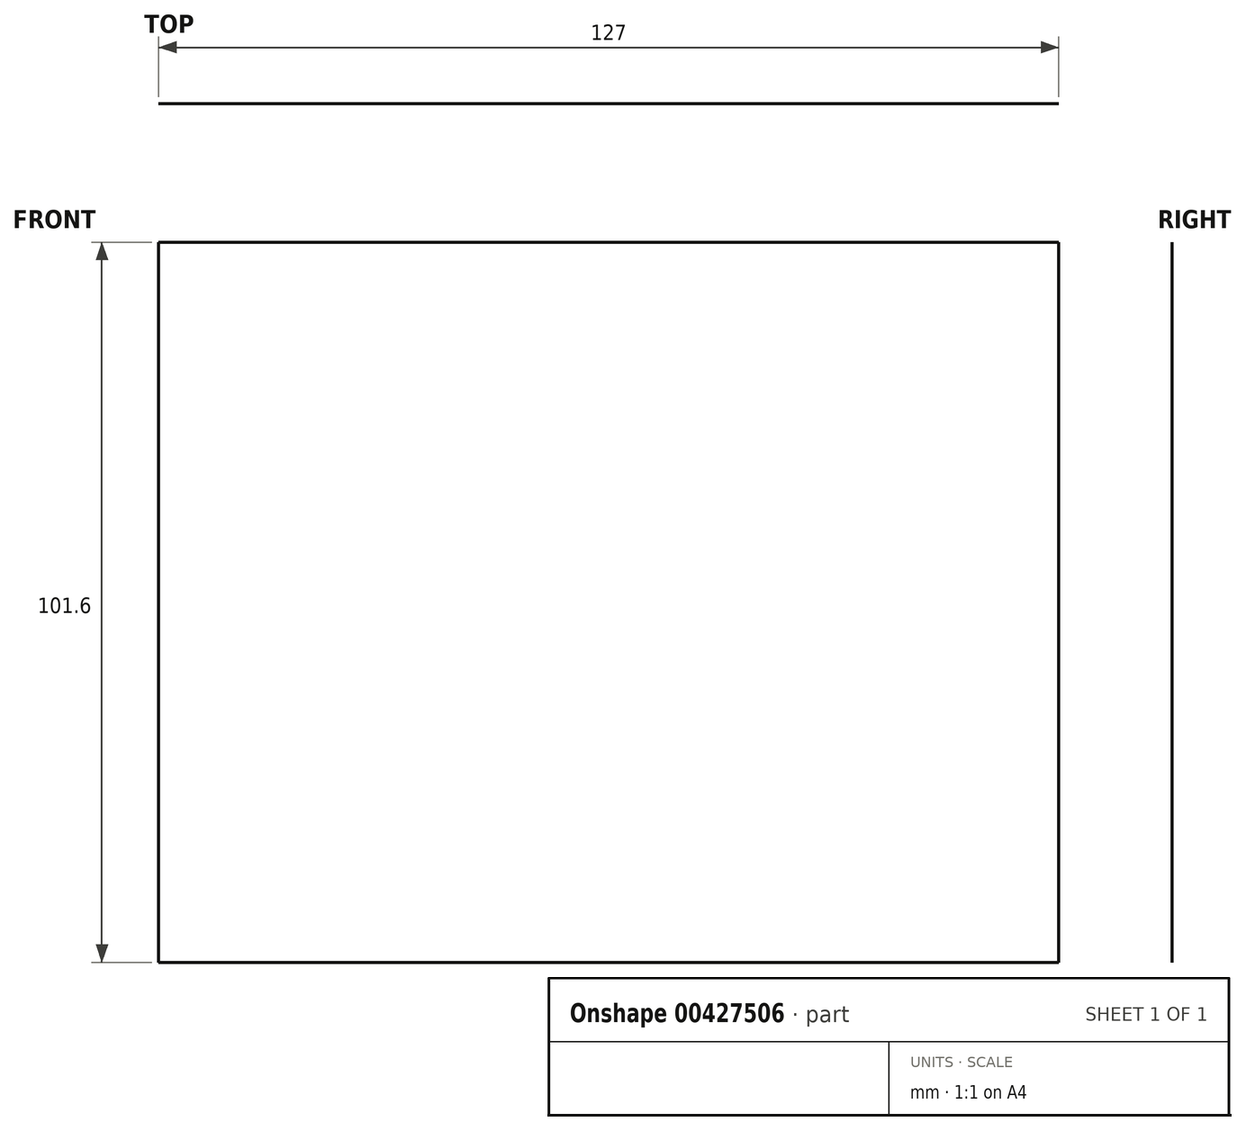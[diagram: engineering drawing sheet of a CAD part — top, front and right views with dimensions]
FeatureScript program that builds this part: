
annotation { "Feature Type Name" : "Feature", "Feature Type Description" : "" }
export const myFeature = defineFeature(function(context is Context, id is Id, definition is map)
    precondition{}
    {
        {
            var Q0;
            Q0=qCreatedBy(makeId("Top.planeOp"),FACE);
            var sketch = newSketch(context, id + "F0", { "sketchPlane" : qUnion([Q0])});
            skLineSegment(sketch, "E0.bottom", {"start": v(-63.5, 1.59) * mm, "end": v(63.5, 1.59) * mm});
            skLineSegment(sketch, "E0.top", {"start": v(-63.5, -1.59) * mm, "end": v(63.5, -1.59) * mm});
            skLineSegment(sketch, "E0.left", {"start": v(-63.5, 1.59) * mm, "end": v(-63.5, -1.59) * mm});
            skLineSegment(sketch, "E0.right", {"start": v(63.5, 1.59) * mm, "end": v(63.5, -1.59) * mm});
            skPoint(sketch, "E0.middle", {"position": v(0, 0) * mm});
            skSolve(sketch);
        }
        {
            var Q0;
            Q0=sQuery(id+"F0.wireOp",EDGE,"E0.top");
            extrude(context, id + "F1", {"bodyType" : ToolBodyType.SURFACE, "surfaceEntities" : qUnion([Q0]), "depth" : 101.6 * mm});
        }
    });
